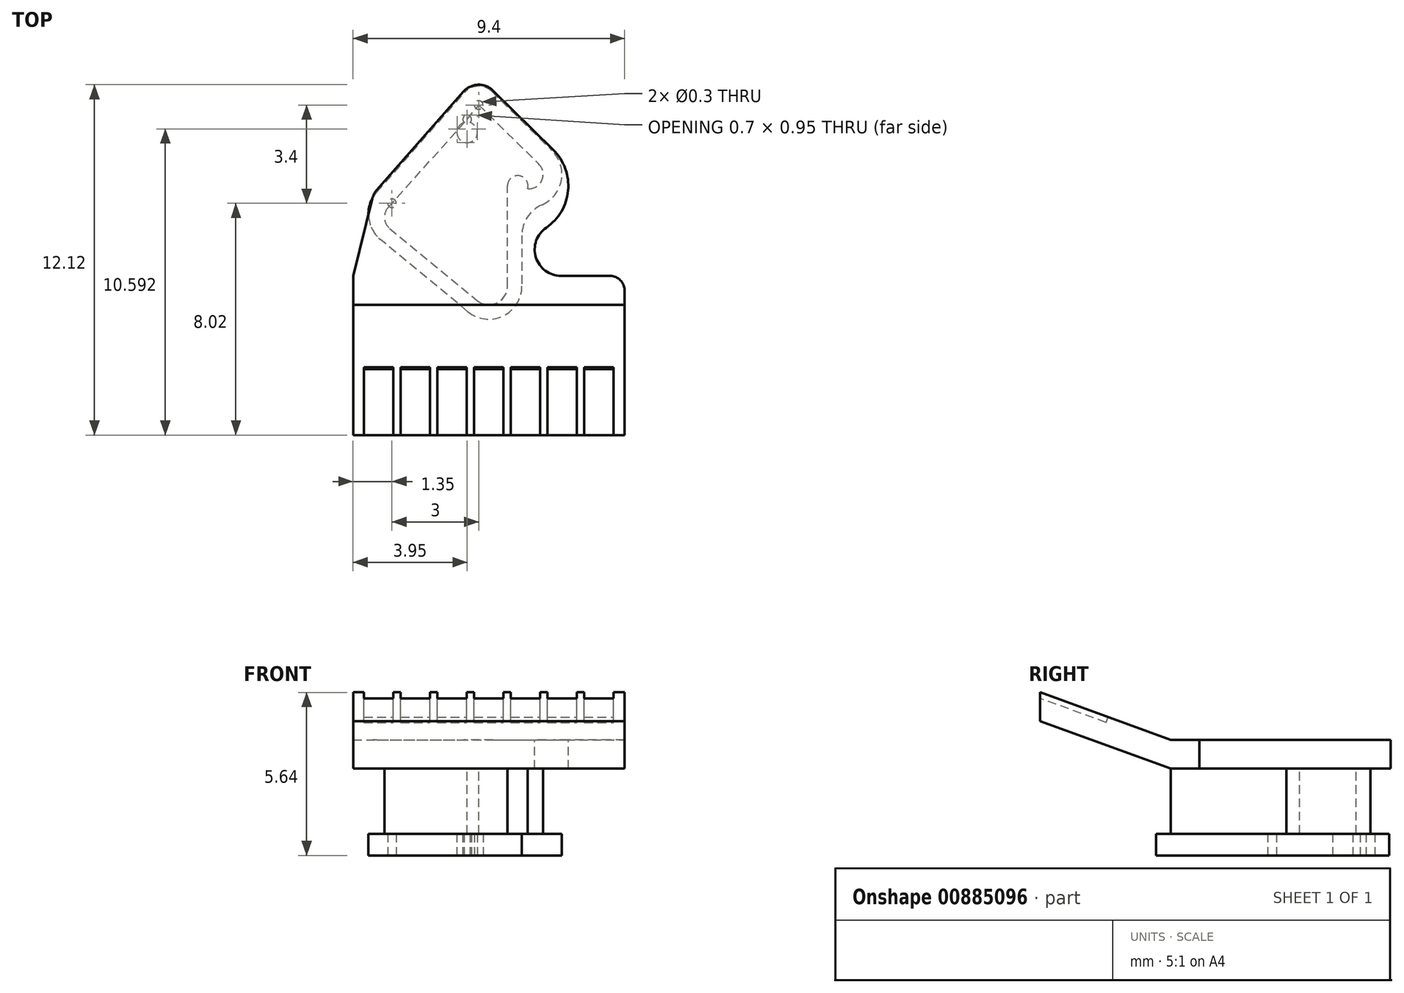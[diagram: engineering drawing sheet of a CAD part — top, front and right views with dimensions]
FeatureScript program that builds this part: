
annotation { "Feature Type Name" : "Feature", "Feature Type Description" : "" }
export const myFeature = defineFeature(function(context is Context, id is Id, definition is map)
    precondition{}
    {
        {
            assignVariable(context, id + "F0", {"name" : "top_height", "anyValue" : 1 * mm});
        }
        {
            assignVariable(context, id + "F1", {"name" : "foot_height", "anyValue" : 0.75 * mm});
        }
        {
            assignVariable(context, id + "F2", {"name" : "total_height", "anyValue" : 4 * mm});
        }
        {
            var Q0;
            Q0=qCreatedBy(makeId("Top.planeOp"),FACE);
            var sketch = newSketch(context, id + "F3", { "sketchPlane" : qUnion([Q0])});
            skCircle(sketch, "E0", {"center": v(-3.35, -1) * mm, "radius": 0.15 * mm});
            skCircle(sketch, "E1", {"center": v(-0.75, 1.9) * mm, "radius": 0.15 * mm});
            skCircle(sketch, "E2", {"center": v(-0.35, 2.4) * mm, "radius": 0.15 * mm});
            skCircle(sketch, "E3", {"center": v(-0.75, 1.45) * mm, "radius": 0.35 * mm});
            skCircle(sketch, "E4", {"center": v(2.5, -2.6) * mm, "radius": 0.85 * mm});
            skSolve(sketch);
        }
        {
            var Q0;
            Q0=qSketchRegion(id+"F3",true);
            extrude(context, id + "F4", {"entities" : qUnion([Q0]), "depth" : getVariable(context, 'total_height')});
        }
        {
            var Q0;
            Q0=makeQuery(id+"F4.opExtrude","CAP_FACE",FACE,{"disambiguationData":[OSD([sQuery(id+"F3.wireOp",EDGE,"E4")])],"isStart":false});
            var sketch = newSketch(context, id + "F5", { "sketchPlane" : qUnion([Q0])});
            skArc(sketch, "E5", {"start": v(2.23, 0.85) * mm, "mid": v(2.74, -0.56) * mm, "end": v(1.99, -1.85) * mm});
            skArc(sketch, "E6", {"start": v(1.99, -1.85) * mm, "mid": v(1.63, -2.87) * mm, "end": v(2.5, -3.51) * mm});
            skArc(sketch, "E7", {"start": v(0.14, 2.9) * mm, "mid": v(-0.37, 3.1) * mm, "end": v(-0.87, 2.86) * mm});
            skArc(sketch, "E8", {"start": v(-4.03, -0.83) * mm, "mid": v(-3.97, -0.67) * mm, "end": v(-3.87, -0.54) * mm});
            skLineSegment(sketch, "E9", {"start": v(-3.87, -0.54) * mm, "end": v(-0.87, 2.86) * mm});
            skLineSegment(sketch, "E10", {"start": v(0.14, 2.9) * mm, "end": v(2.23, 0.85) * mm});
            skLineSegment(sketch, "E11", {"start": v(-4.7, -4.51) * mm, "end": v(4.7, -4.51) * mm});
            skLineSegment(sketch, "E12", {"start": v(-4.7, -4.51) * mm, "end": v(-4.7, -3.51) * mm});
            skLineSegment(sketch, "E13", {"start": v(-4.7, -3.51) * mm, "end": v(-4.03, -0.83) * mm});
            skLineSegment(sketch, "E14", {"start": v(4.7, -4.51) * mm, "end": v(4.7, -4.01) * mm});
            skLineSegment(sketch, "E15", {"start": v(4.2, -3.51) * mm, "end": v(2.5, -3.51) * mm});
            skPoint(sketch, "E16.visualSharp", {"position": v(4.7, -3.51) * mm});
            skArc(sketch, "E16.filletArc", {"start": v(4.7, -4.01) * mm, "mid": v(4.55, -3.66) * mm, "end": v(4.2, -3.51) * mm});
            skLineSegment(sketch, "E17", {"start": v(4.7, -3.51) * mm, "end": v(4.7, -4.51) * mm, "construction": true});
            skSolve(sketch);
        }
        {
            var Q0;
            Q0=qSketchRegion(id+"F5",true);
            extrude(context, id + "F6", {"entities" : qUnion([Q0]), "oppositeDirection" : true, "depth" : getVariable(context, 'top_height')});
        }
        {
            var Q0;
            Q0=makeQuery(id+"F6.opExtrude","CAP_FACE",FACE,{"disambiguationData":[OSD([sQuery(id+"F5.wireOp",EDGE,"E5"),sQuery(id+"F5.wireOp",EDGE,"E6"),sQuery(id+"F5.wireOp",EDGE,"E7"),sQuery(id+"F5.wireOp",EDGE,"E8"),sQuery(id+"F5.wireOp",EDGE,"E9"),sQuery(id+"F5.wireOp",EDGE,"E10"),sQuery(id+"F5.wireOp",EDGE,"E11"),sQuery(id+"F5.wireOp",EDGE,"E12"),sQuery(id+"F5.wireOp",EDGE,"E13"),sQuery(id+"F5.wireOp",EDGE,"E14"),sQuery(id+"F5.wireOp",EDGE,"E15"),sQuery(id+"F5.wireOp",EDGE,"E16.filletArc")])],"isStart":false});
            var sketch = newSketch(context, id + "F7", { "sketchPlane" : qUnion([Q0])});
            skArc(sketch, "E18", {"start": v(-0.41, 4.36) * mm, "mid": v(0.27, 4.45) * mm, "end": v(0.64, 3.87) * mm});
            skLineSegment(sketch, "E19", {"start": v(0.64, 3.87) * mm, "end": v(0.64, 0.4) * mm});
            skArc(sketch, "E20", {"start": v(0.64, 0.4) * mm, "mid": v(1.05, 0.05) * mm, "end": v(1.34, 0.5) * mm});
            skLineSegment(sketch, "E21", {"start": v(-3.48, 1.15) * mm, "end": v(-0.75, -1.9) * mm});
            skPoint(sketch, "E22", {"position": v(-3.35, 1) * mm});
            skPoint(sketch, "E23", {"position": v(-0.75, -1.9) * mm});
            skPoint(sketch, "E24", {"position": v(-0.35, -2.4) * mm});
            skLineSegment(sketch, "E25", {"start": v(-0.75, -1.9) * mm, "end": v(-0.35, -2.4) * mm});
            skArc(sketch, "E26", {"start": v(-3.48, 1.15) * mm, "mid": v(-3.6, 1.52) * mm, "end": v(-3.43, 1.87) * mm});
            skLineSegment(sketch, "E27", {"start": v(-3.43, 1.87) * mm, "end": v(-0.41, 4.36) * mm});
            skArc(sketch, "E28", {"start": v(1.38, 0.5) * mm, "mid": v(1.84, 0.19) * mm, "end": v(1.73, -0.36) * mm});
            skLineSegment(sketch, "E29", {"start": v(-0.35, -2.4) * mm, "end": v(1.73, -0.36) * mm});
            skLineSegment(sketch, "E30", {"start": v(1.38, 0.5) * mm, "end": v(1.34, 0.5) * mm});
            skSolve(sketch);
        }
        {
            var Q0;
            Q0=qSketchRegion(id+"F7",true);
            extrude(context, id + "F8", {"entities" : qUnion([Q0]), "depth" : getVariable(context, 'total_height') - getVariable(context, 'top_height') - getVariable(context, 'foot_height')});
        }
        {
            var Q0;
            Q0=makeQuery(id+"F8.opExtrude","CAP_FACE",FACE,{"disambiguationData":[OSD([sQuery(id+"F7.wireOp",EDGE,"E18"),sQuery(id+"F7.wireOp",EDGE,"E19"),sQuery(id+"F7.wireOp",EDGE,"E20"),sQuery(id+"F7.wireOp",EDGE,"E21"),sQuery(id+"F7.wireOp",EDGE,"E25"),sQuery(id+"F7.wireOp",EDGE,"E26"),sQuery(id+"F7.wireOp",EDGE,"E27"),sQuery(id+"F7.wireOp",EDGE,"E28"),sQuery(id+"F7.wireOp",EDGE,"E29"),sQuery(id+"F7.wireOp",EDGE,"E30")])],"isStart":false});
            var sketch = newSketch(context, id + "F9", { "sketchPlane" : qUnion([Q0])});
            skLineSegment(sketch, "E31", {"start": v(-3.88, 0.62) * mm, "end": v(-0.84, -2.83) * mm});
            skLineSegment(sketch, "E32", {"start": v(0.1, -2.86) * mm, "end": v(2.18, -0.82) * mm});
            skLineSegment(sketch, "E33", {"start": v(1.14, 2.1) * mm, "end": v(1.14, 3.87) * mm});
            skLineSegment(sketch, "E34", {"start": v(-0.73, 4.75) * mm, "end": v(-3.75, 2.25) * mm});
            skArc(sketch, "E35.filletArc", {"start": v(-3.75, 2.25) * mm, "mid": v(-4.16, 1.46) * mm, "end": v(-3.88, 0.62) * mm});
            skPoint(sketch, "E36.visualSharp", {"position": v(1.14, 6.3) * mm});
            skArc(sketch, "E36.filletArc", {"start": v(1.15, 3.87) * mm, "mid": v(0.49, 4.9) * mm, "end": v(-0.73, 4.75) * mm});
            skArc(sketch, "E37.filletArc", {"start": v(2.18, -0.82) * mm, "mid": v(2.5, 0.2) * mm, "end": v(1.84, 1.05) * mm});
            skArc(sketch, "E38.filletArc", {"start": v(1.15, 2.1) * mm, "mid": v(1.33, 1.48) * mm, "end": v(1.84, 1.05) * mm});
            skPoint(sketch, "E39.visualSharp", {"position": v(-0.38, -3.34) * mm});
            skArc(sketch, "E39.filletArc", {"start": v(-0.84, -2.83) * mm, "mid": v(-0.37, -3.05) * mm, "end": v(0.1, -2.86) * mm});
            skSolve(sketch);
        }
        {
            var Q0;
            Q0=qSketchRegion(id+"F9",true);
            extrude(context, id + "F10", {"entities" : qUnion([Q0]), "depth" : getVariable(context, 'foot_height')});
        }
        {
            var Q0;
            Q0=makeQuery(id+"F4.opExtrude","SWEPT_BODY",BODY,{"disambiguationData":[OSD([sQuery(id+"F3.wireOp",EDGE,"E0")])]});
            var Q1;
            Q1=makeQuery(id+"F4.opExtrude","SWEPT_BODY",BODY,{"disambiguationData":[OSD([sQuery(id+"F3.wireOp",EDGE,"E1")])]});
            var Q2;
            Q2=makeQuery(id+"F4.opExtrude","SWEPT_BODY",BODY,{"disambiguationData":[OSD([sQuery(id+"F3.wireOp",EDGE,"E2")])]});
            var Q3;
            Q3=makeQuery(id+"F4.opExtrude","SWEPT_BODY",BODY,{"disambiguationData":[OSD([sQuery(id+"F3.wireOp",EDGE,"E3")])]});
            var Q4;
            Q4=makeQuery(id+"F4.opExtrude","SWEPT_BODY",BODY,{"disambiguationData":[OSD([sQuery(id+"F3.wireOp",EDGE,"E4")])]});
            var Q5;
            Q5=makeQuery(id+"F10.opExtrude","SWEPT_BODY",BODY,{"disambiguationData":[OSD([sQuery(id+"F9.wireOp",EDGE,"E31"),sQuery(id+"F9.wireOp",EDGE,"E32"),sQuery(id+"F9.wireOp",EDGE,"E33"),sQuery(id+"F9.wireOp",EDGE,"E34"),sQuery(id+"F9.wireOp",EDGE,"E35.filletArc"),sQuery(id+"F9.wireOp",EDGE,"E36.filletArc"),sQuery(id+"F9.wireOp",EDGE,"E37.filletArc"),sQuery(id+"F9.wireOp",EDGE,"E38.filletArc"),sQuery(id+"F9.wireOp",EDGE,"E39.filletArc")])]});
            booleanBodies(context, id + "F11", {"operationType" : BooleanOperationType.SUBTRACTION, "tools" : qUnion([Q0, Q1, Q2, Q3, Q4]), "targets" : qUnion([Q5])});
        }
        {
            var Q0;
            Q0=qCreatedBy(makeId("Right.planeOp"),FACE);
            var sketch = newSketch(context, id + "F12", { "sketchPlane" : qUnion([Q0])});
            skLineSegment(sketch, "E40", {"start": v(-9.02, 5.64) * mm, "end": v(-4.51, 4) * mm});
            skSolve(sketch);
        }
        {
            var Q0;
            Q0=makeQuery(id+"F6.opExtrude","SWEPT_FACE",FACE,{"disambiguationData":[OSD([sQuery(id+"F5.wireOp",EDGE,"E11")])]});
            var Q1;
            Q1=sQuery(id+"F12.wireOp",EDGE,"E40");
            sweep(context, id + "F13", {"operationType" : NewBodyOperationType.ADD, "profiles" : qUnion([Q0]), "path" : qUnion([Q1]), "keepProfileOrientation" : true});
        }
        {
            var Q0;
            {var subQ0=sQuery(id+"F12.wireOp",EDGE,"E40");var subQ1=sQuery(id+"F5.wireOp",EDGE,"E11");Q0=makeQuery(id+"F13.opSweep","SWEPT_FACE",FACE,{"disambiguationData":[OSD([subQ1,subQ0]),TDD([makeQuery(id+"F6.opExtrude","CAP_EDGE",EDGE,{"disambiguationData":[OSD([subQ1])],"isStart":true}),subQ0])]});}
            var sketch = newSketch(context, id + "F14", { "sketchPlane" : qUnion([Q0])});
            skLineSegment(sketch, "E41.bottom", {"start": v(-4.32, -7.9) * mm, "end": v(-3.3, -7.9) * mm});
            skLineSegment(sketch, "E41.top", {"start": v(-4.32, -10.4) * mm, "end": v(-3.3, -10.4) * mm});
            skLineSegment(sketch, "E41.left", {"start": v(-4.32, -7.9) * mm, "end": v(-4.32, -10.4) * mm});
            skLineSegment(sketch, "E41.right", {"start": v(-3.3, -7.9) * mm, "end": v(-3.3, -10.4) * mm});
            skLineSegment(sketch, "E42.1.0.0", {"start": v(-3.05, -7.9) * mm, "end": v(-3.05, -10.4) * mm});
            skLineSegment(sketch, "E42.1.0.1", {"start": v(-3.05, -7.9) * mm, "end": v(-2.03, -7.9) * mm});
            skLineSegment(sketch, "E42.1.0.2", {"start": v(-2.03, -7.9) * mm, "end": v(-2.03, -10.4) * mm});
            skLineSegment(sketch, "E42.1.0.3", {"start": v(-3.05, -10.4) * mm, "end": v(-2.03, -10.4) * mm});
            skLineSegment(sketch, "E42.2.0.0", {"start": v(-1.78, -7.9) * mm, "end": v(-1.78, -10.4) * mm});
            skLineSegment(sketch, "E42.2.0.1", {"start": v(-1.78, -7.9) * mm, "end": v(-0.76, -7.9) * mm});
            skLineSegment(sketch, "E42.2.0.2", {"start": v(-0.76, -7.9) * mm, "end": v(-0.76, -10.4) * mm});
            skLineSegment(sketch, "E42.2.0.3", {"start": v(-1.78, -10.4) * mm, "end": v(-0.76, -10.4) * mm});
            skLineSegment(sketch, "E42.3.0.0", {"start": v(-0.51, -7.9) * mm, "end": v(-0.51, -10.4) * mm});
            skLineSegment(sketch, "E42.3.0.1", {"start": v(-0.5, -7.9) * mm, "end": v(0.51, -7.9) * mm});
            skLineSegment(sketch, "E42.3.0.2", {"start": v(0.51, -7.9) * mm, "end": v(0.51, -10.4) * mm});
            skLineSegment(sketch, "E42.3.0.3", {"start": v(-0.5, -10.4) * mm, "end": v(0.51, -10.4) * mm});
            skLineSegment(sketch, "E42.4.0.0", {"start": v(0.76, -7.9) * mm, "end": v(0.76, -10.4) * mm});
            skLineSegment(sketch, "E42.4.0.1", {"start": v(0.76, -7.9) * mm, "end": v(1.78, -7.9) * mm});
            skLineSegment(sketch, "E42.4.0.2", {"start": v(1.78, -7.9) * mm, "end": v(1.78, -10.4) * mm});
            skLineSegment(sketch, "E42.4.0.3", {"start": v(0.76, -10.4) * mm, "end": v(1.78, -10.4) * mm});
            skLineSegment(sketch, "E42.5.0.0", {"start": v(2.03, -7.9) * mm, "end": v(2.03, -10.4) * mm});
            skLineSegment(sketch, "E42.5.0.1", {"start": v(2.03, -7.9) * mm, "end": v(3.05, -7.9) * mm});
            skLineSegment(sketch, "E42.5.0.2", {"start": v(3.05, -7.9) * mm, "end": v(3.05, -10.4) * mm});
            skLineSegment(sketch, "E42.5.0.3", {"start": v(2.03, -10.4) * mm, "end": v(3.05, -10.4) * mm});
            skLineSegment(sketch, "E42.6.0.0", {"start": v(3.3, -7.9) * mm, "end": v(3.3, -10.4) * mm});
            skLineSegment(sketch, "E42.6.0.1", {"start": v(3.3, -7.9) * mm, "end": v(4.32, -7.9) * mm});
            skLineSegment(sketch, "E42.6.0.2", {"start": v(4.32, -7.9) * mm, "end": v(4.32, -10.4) * mm});
            skLineSegment(sketch, "E42.6.0.3", {"start": v(3.3, -10.4) * mm, "end": v(4.32, -10.4) * mm});
            skLineSegment(sketch, "E42.direction1", {"start": v(-4.32, -10.4) * mm, "end": v(-3.05, -10.4) * mm, "construction": true});
            skSolve(sketch);
        }
        {
            var Q0;
            Q0=qSketchRegion(id+"F14",true);
            extrude(context, id + "F15", {"entities" : qUnion([Q0]), "operationType" : NewBodyOperationType.REMOVE, "oppositeDirection" : true, "depth" : 0.2 * mm});
        }
    });
